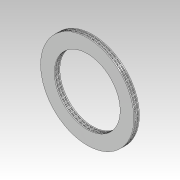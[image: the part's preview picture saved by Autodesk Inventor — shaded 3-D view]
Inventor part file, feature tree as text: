
AUTODESK INVENTOR PART (.ipt)
format: ipt  version: 2020 (Build 240168000, 168)  size: 623,616 bytes
history: native  units: mm
features: sketch x3, revolve x2, extrude x1, pattern_circular x1
ambient origin geometry x8: Origin, YZ Plane, XZ Plane, XY Plane, X Axis, Y Axis, Z Axis, Center Point
bodies: Solid1 (feature_tree)
feature tree (7):
  extrude  "Extrusion1"  Depth=60.0mm
  revolve  "Revolution1"  [1 undecoded]
  pattern_circular  "Circular Pattern1"  Count=50 Angle=360.0deg
  revolve  "Revolution2"  [1 undecoded]
  sketch  "Sketch1"  dims[d0=60.0mm d1=85.0mm]
  sketch  "Sketch2"  dims[d2=1.0mm d3=0.0mm d4=1.5mm]
  sketch  "Sketch3"  dims[d5=90.0deg d6=500.0mm d7=360.0deg d9=1.0mm d10=1.0mm d11=90.0deg]
note: 2 required parameter values undecoded (feature->parameter linkage not recoverable at this tier; creation-order binding heuristic only, values carry confidence <= 0.55)
